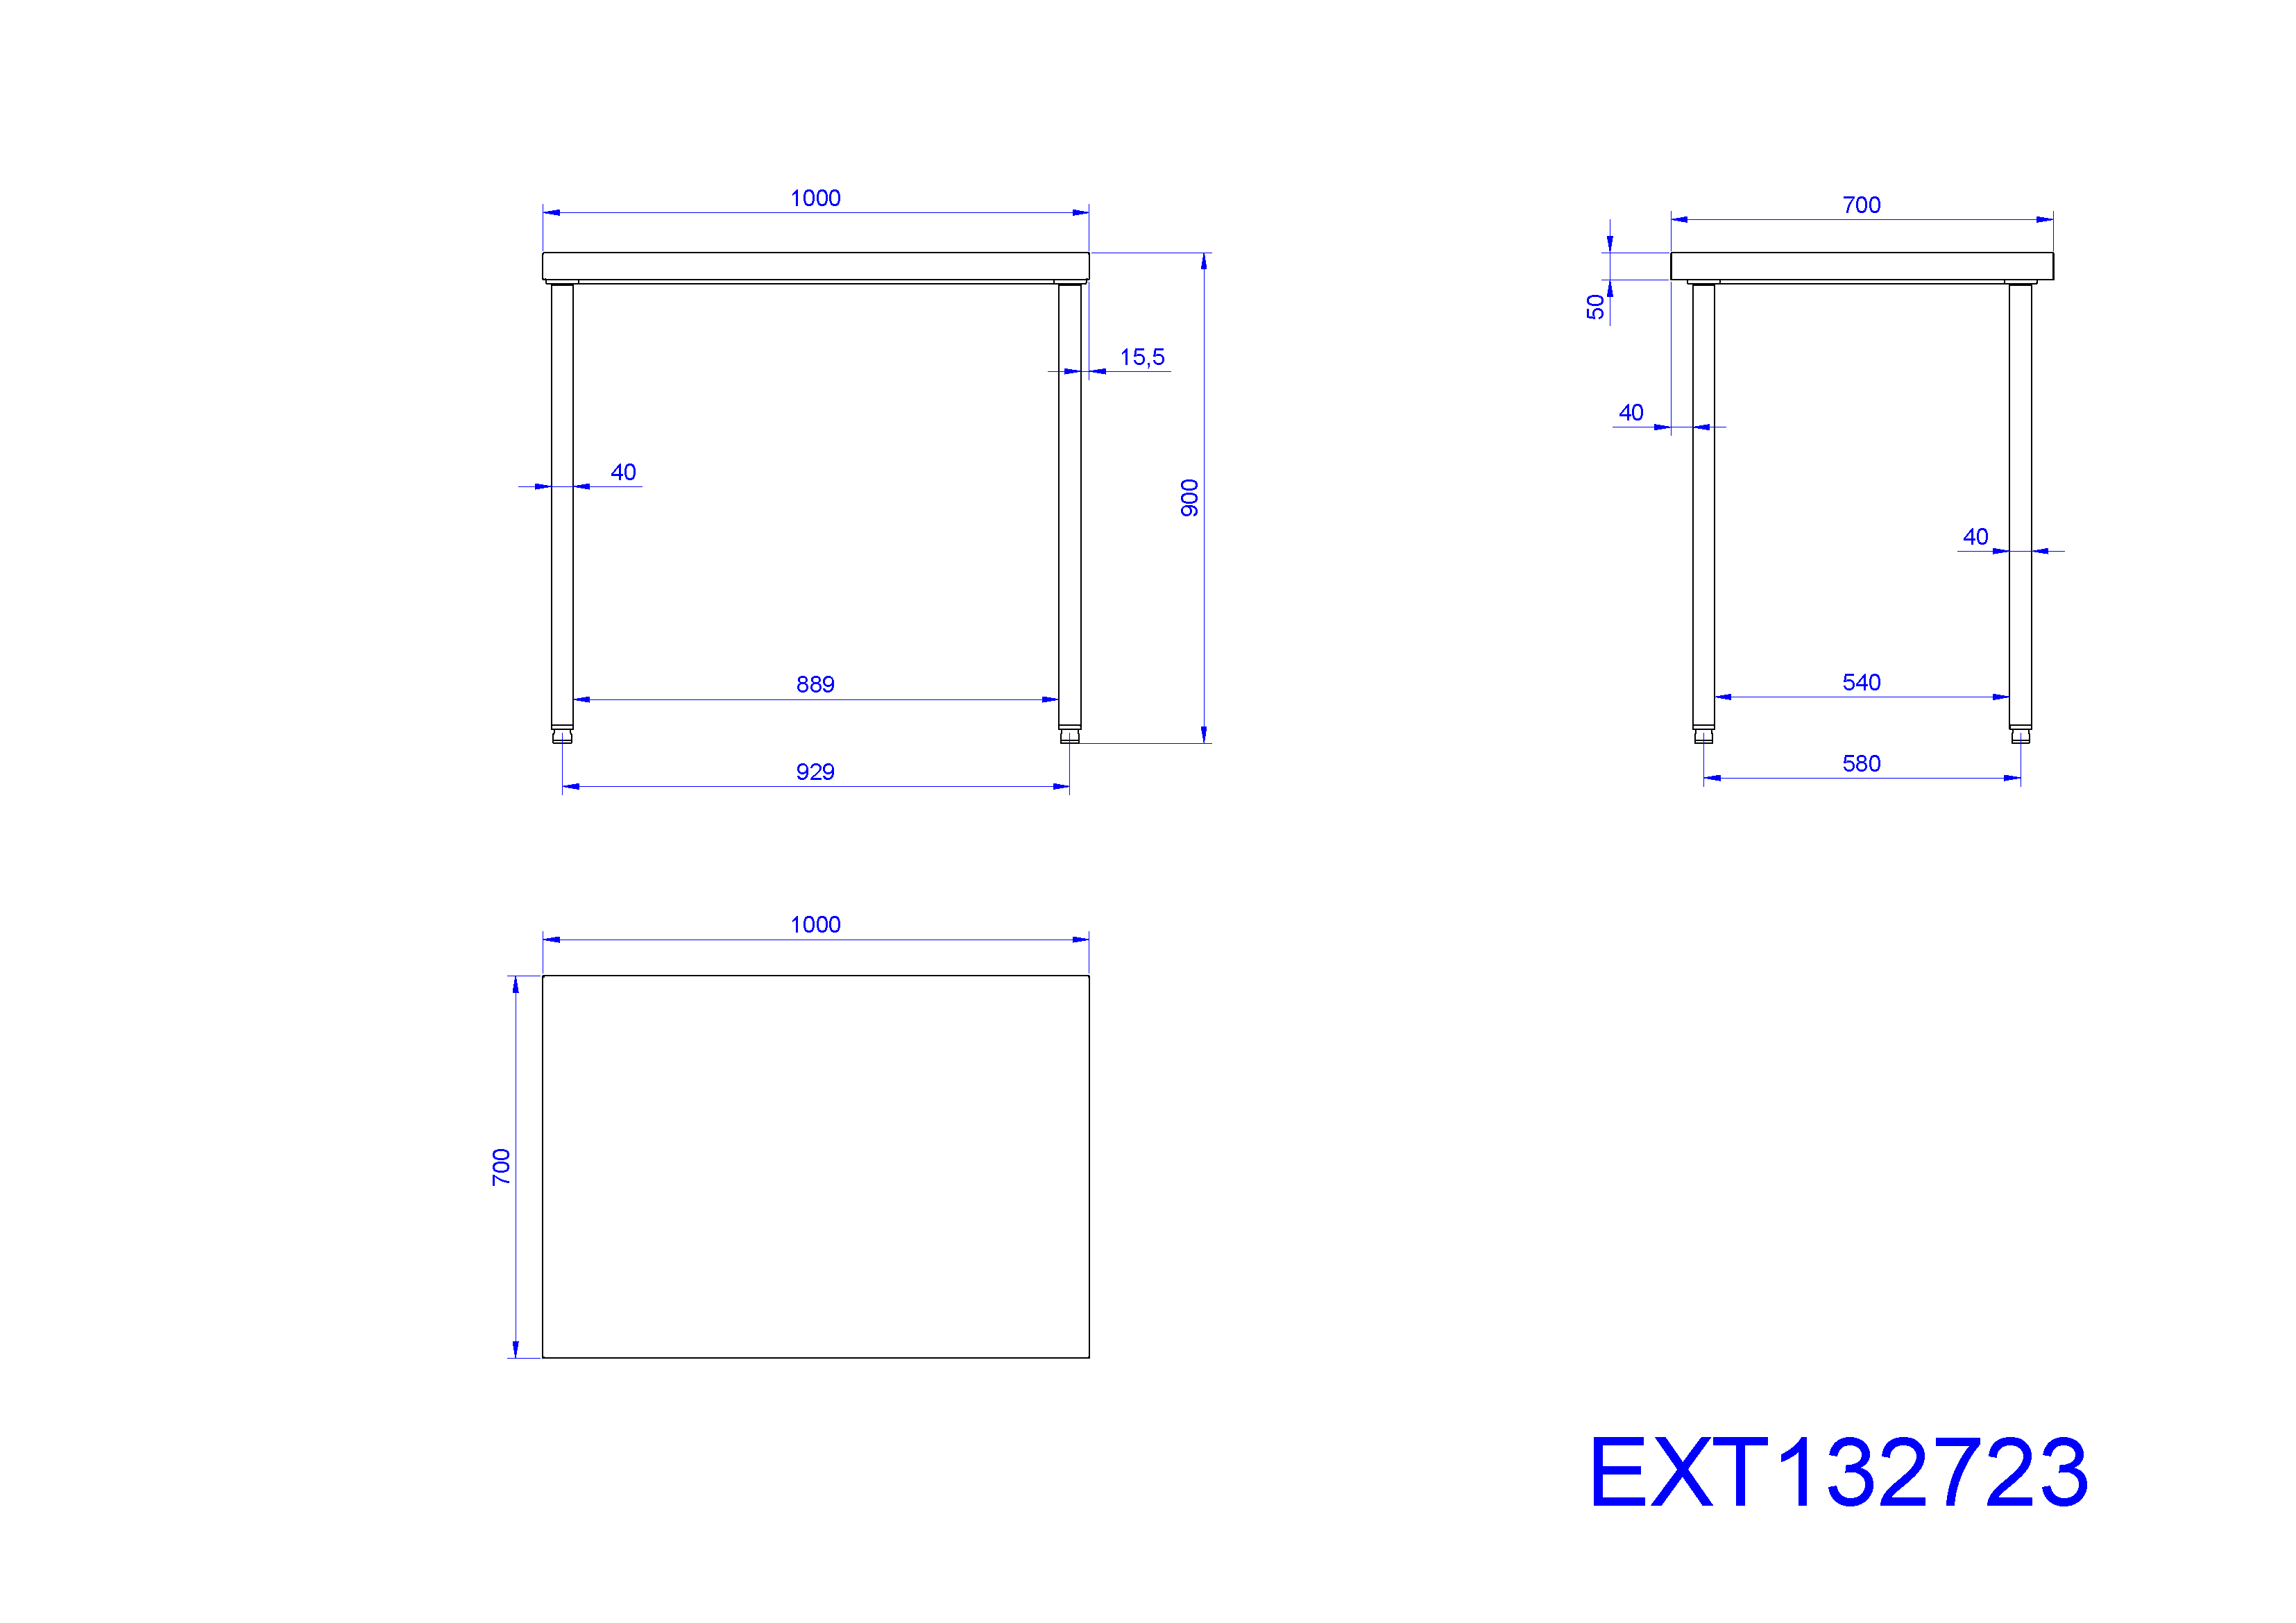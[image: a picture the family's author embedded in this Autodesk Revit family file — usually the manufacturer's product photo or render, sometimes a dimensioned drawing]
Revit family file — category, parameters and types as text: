
# Revit family: QF_ELECTROLUXPROFESSIONAL_133051_TG1600EN
name_source: partatom
category: Attrezzature speciali
units: mm (PartAtom-declared; Revit-internal decimal feet)

## family parameters
Basato su piano di lavoro = No
Condiviso = No
Punto di calcolo locali = No
Quota connettore circolare = Usa diametro
Sempre verticale = Sì
Taglio con vuoti quando caricato = No
Tipo di parte = Normale

## types (1)
- Standard
    Accessory = Sì
    Cold Water Size = 0 mm
    Compressed Air Pressure = 0.0 Pa
    Compressed Air Size = 0 mm
    Compressed Air Volume = 0.0 L/s
    Condensate Return Size = 0 mm
    Cycle = 0 Hz
    Depth Actual = 700 mm  [stored 2.29659 ft]
    Descrizione = WORK TABLE 1600 MM
    Direct Waste Size = 0 mm
    Gas Input Pressure = 0
    Gas KW = 0
    Gas Size = 0 mm
    HP = 0 HP
    Height Actual = 900 mm  [stored 2.95276 ft]
    Hot Water Size = 0 mm
    Item Number = 133051
    Length Actual = 1600 mm  [stored 5.24934 ft]
    Modello = TG1600EN
    Phase = 0
    Produttore = Electrolux Professional
    Prospetto di default = 0 mm  [stored 0 ft]
    Refrigerant Compressor Remote = Sì
    Refrigeration Liquid Line Size = 0 mm  [stored 0 ft]
    Refrigeration Suction Line Size = 0 mm  [stored 0 ft]
    Steam Consumption per Hour = 0
    Steam Supply Maximum Pressure = 0.0 Pa
    Steam Supply Minimum Pressure = 0.0 Pa
    Steam Supply Size = 0 mm
    URL = https://www.electroluxprofessional.com
    URL Manufacturer = https://www.electroluxprofessional.com
    Volts = 0 V
    Watts = 0 W
    Weight = 50.00 kg

note: source unit labels omitted for Gas Input Pressure — the stored unit's dimension contradicts the parameter name (converter mislabeling)

note: [stored X ft] marks values corroborated as IEEE doubles in the binary element streams (Revit-internal decimal feet)

## geometry (parser evidence)
native form markers: Sweep x2
no freeform markers — native parametric forms only
